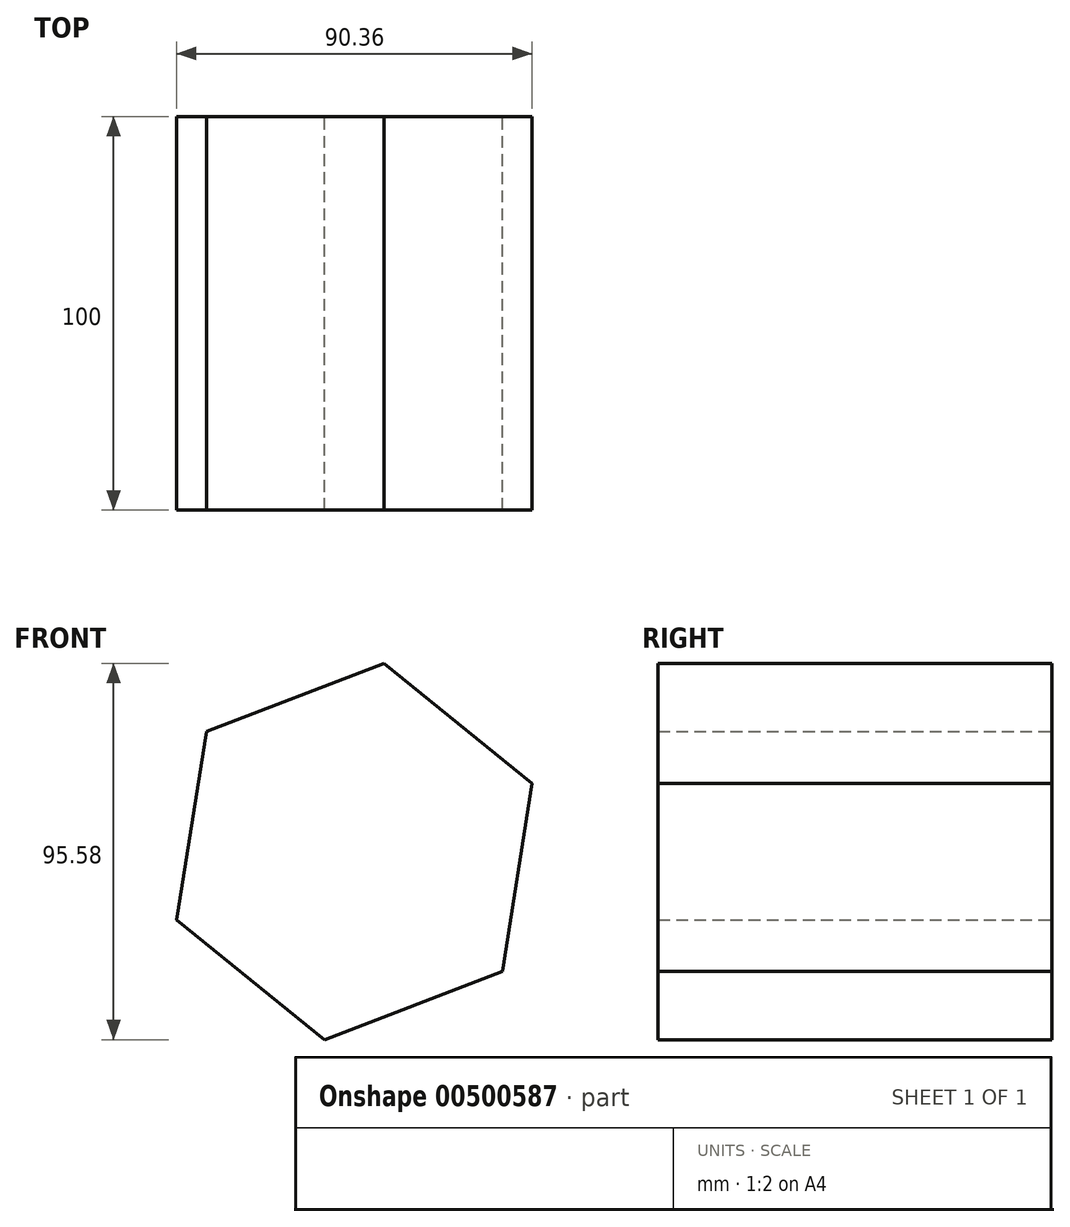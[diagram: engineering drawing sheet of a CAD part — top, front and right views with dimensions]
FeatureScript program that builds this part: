
annotation { "Feature Type Name" : "Feature", "Feature Type Description" : "" }
export const myFeature = defineFeature(function(context is Context, id is Id, definition is map)
    precondition{}
    {
        {
            var Q0;
            Q0=qCreatedBy(makeId("Front.planeOp"),FACE);
            var sketch = newSketch(context, id + "F0", { "sketchPlane" : qUnion([Q0])});
            skCircle(sketch, "E0.cCircle", {"center": v(0, 0) * mm, "radius": 48.39 * mm, "construction": true});
            skLineSegment(sketch, "E0.0", {"start": v(-37.6, 30.46) * mm, "end": v(7.58, 47.8) * mm});
            skLineSegment(sketch, "E0.1", {"start": v(7.58, 47.8) * mm, "end": v(45.18, 17.33) * mm});
            skLineSegment(sketch, "E0.2", {"start": v(45.18, 17.33) * mm, "end": v(37.6, -30.46) * mm});
            skLineSegment(sketch, "E0.3", {"start": v(37.6, -30.46) * mm, "end": v(-7.58, -47.8) * mm});
            skLineSegment(sketch, "E0.4", {"start": v(-7.58, -47.8) * mm, "end": v(-45.18, -17.33) * mm});
            skLineSegment(sketch, "E0.5", {"start": v(-45.18, -17.33) * mm, "end": v(-37.6, 30.46) * mm});
            skSolve(sketch);
        }
        {
            var Q0;
            Q0=makeQuery(id+"F0.imprint","IMPRINT",FACE,{"disambiguationData":[TD([[makeQuery(id+"F0.imprint","IMPRINT",EDGE,{"derivedFrom":sQuery(id+"F0.wireOp",EDGE,"E0.0")}),-1.0]])]});
            extrude(context, id + "F1", {"entities" : qUnion([Q0]), "endBound" : BoundingType.SYMMETRIC, "depth" : 100 * mm});
        }
    });
